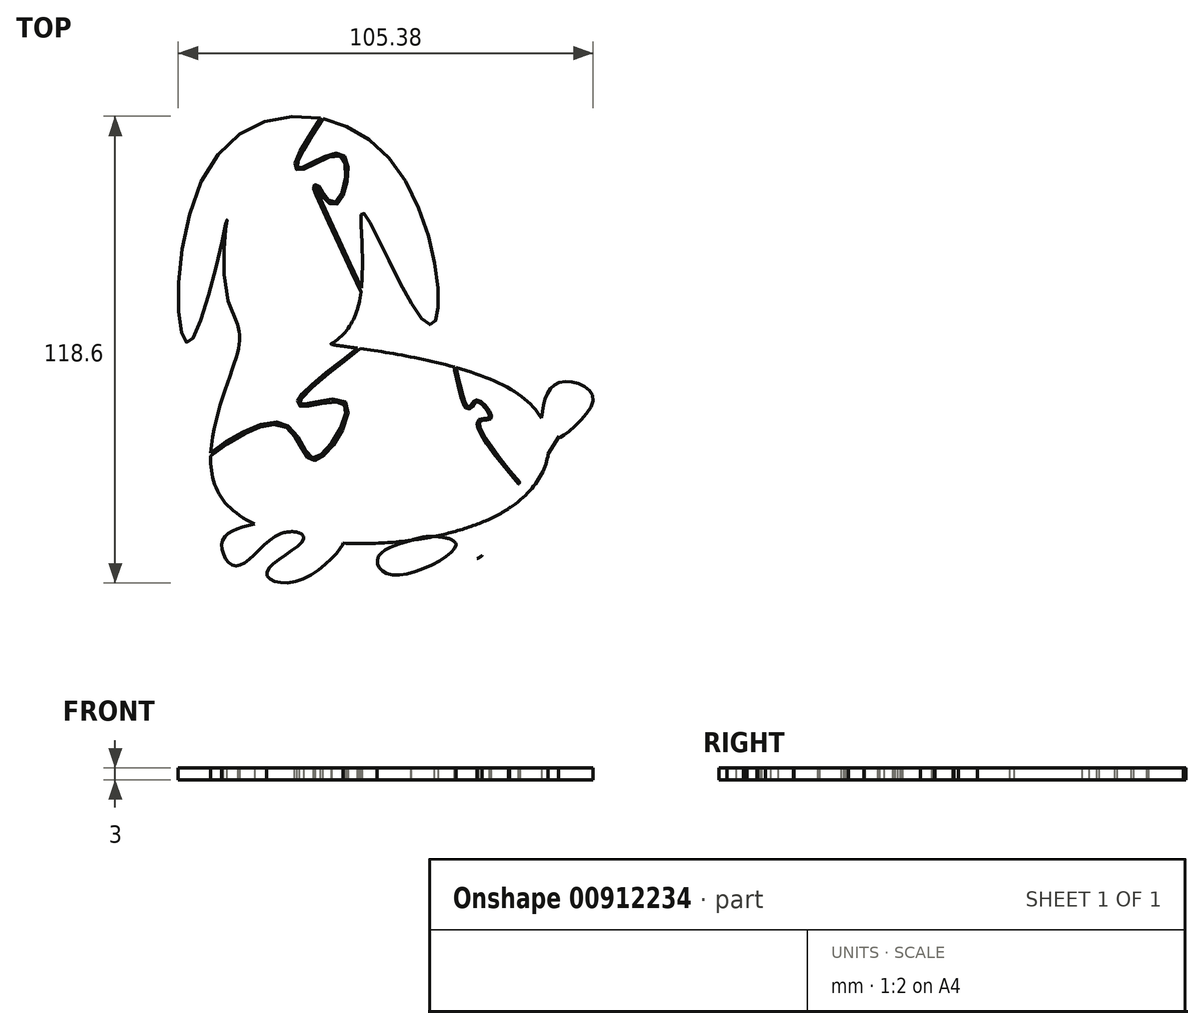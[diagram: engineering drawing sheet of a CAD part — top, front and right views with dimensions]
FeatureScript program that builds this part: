
annotation { "Feature Type Name" : "Feature", "Feature Type Description" : "" }
export const myFeature = defineFeature(function(context is Context, id is Id, definition is map)
    precondition{}
    {
        {
            var Q0;
            Q0=qCreatedBy(makeId("Top.planeOp"),FACE);
            var sketch = newSketch(context, id + "F0", { "sketchPlane" : qUnion([Q0])});
            skFitSpline(sketch, "E0", {"points": [v(-42.08, 41.4) * mm, v(3.83, 40.95) * mm, v(12.83, 0) * mm, v(-3.83, 28.35) * mm, v(-6.98, 0) * mm, v(-35.78, 0) * mm, v(-38.48, 26.55) * mm, v(-47.93, -4.5) * mm, v(-42.08, 41.4) * mm]});
            skFitSpline(sketch, "E1", {"points": [v(-35.78, 0) * mm, v(-35.78, -7.26) * mm, v(-39.63, -44.35) * mm, v(33.41, -46.62) * mm, v(36.82, -18.62) * mm, v(-12.02, -5) * mm, v(-11.88, -4.9) * mm], "startDerivative": vector(15.72, -60) * mm, "endDerivative": vector(20.6, 2.21) * mm});
            skFitSpline(sketch, "E2", {"points": [v(41.44, -23.83) * mm, v(45.9, -14.83) * mm, v(54.6, -19) * mm, v(45.9, -28.84) * mm, v(45.9, -28.46) * mm], "startDerivative": vector(5.67, 39.4) * mm, "endDerivative": vector(3.46, 9.42) * mm});
            skFitSpline(sketch, "E3", {"points": [v(27.3, -49.9) * mm, v(19.79, -56.08) * mm, v(25.08, -59.5) * mm, v(33.41, -46.62) * mm, v(28.87, -54.57) * mm], "startDerivative": vector(-46.04, -22.15) * mm, "endDerivative": vector(-28.83, -55.13) * mm});
            skFitSpline(sketch, "E4", {"points": [v(45.9, -28.46) * mm, v(43.2, -32.87) * mm], "startDerivative": vector(-2.71, -4.4) * mm, "endDerivative": vector(-2.71, -4.4) * mm});
            skFitSpline(sketch, "E5", {"points": [v(8.29, -54.86) * mm, v(0, -59.11) * mm, v(3.51, -63.65) * mm, v(19.79, -56.08) * mm, v(14.24, -53.87) * mm, v(8.29, -54.86) * mm]});
            skFitSpline(sketch, "E6", {"points": [v(-31.44, -50.7) * mm, v(-39.63, -55.33) * mm, v(-36.22, -61.38) * mm, v(-24.7, -53.18) * mm, v(-18.93, -54.48) * mm, v(-28.28, -62.9) * mm, v(-20.33, -65.17) * mm, v(-8.87, -55.58) * mm, v(-9.31, -55.56) * mm], "startDerivative": vector(-84.42, -21.79) * mm, "endDerivative": vector(-21.17, -5.05) * mm});
            skLineSegment(sketch, "E7.bottom", {"start": v(-54.76, 55.76) * mm, "end": v(61.05, 55.76) * mm});
            skLineSegment(sketch, "E7.top", {"start": v(-54.76, -68.06) * mm, "end": v(61.05, -68.06) * mm});
            skLineSegment(sketch, "E7.left", {"start": v(-54.76, 55.76) * mm, "end": v(-54.76, -68.06) * mm});
            skLineSegment(sketch, "E7.right", {"start": v(61.05, 55.76) * mm, "end": v(61.05, -68.06) * mm});
            skFitSpline(sketch, "E8", {"points": [v(28.87, -54.57) * mm, v(25.08, -59.5) * mm, v(19.79, -56.08) * mm], "startDerivative": vector(-6.86, -14.03) * mm, "endDerivative": vector(-11.3, 10.97) * mm});
            skSolve(sketch);
        }
        {
            var Q0;
            {var subQ0=sQuery(id+"F0.wireOp",EDGE,"E1");var subQ1=sQuery(id+"F0.wireOp",EDGE,"E0");var subQ2=makeQuery(id+"F0.imprint","INTERSECT",VERTEX,{"disambiguationData":[OD(0.0)],"derivedFrom":[subQ1,subQ0]});Q0=makeQuery(id+"F0.imprint","IMPRINT",FACE,{"disambiguationData":[TD([[makeQuery(id+"F0.imprint","IMPRINT",EDGE,{"disambiguationData":[TD([[subQ2,1.0]])],"derivedFrom":subQ1}),-1.0]])]});}
            var Q1;
            {var subQ0=sQuery(id+"F0.wireOp",EDGE,"E1");var subQ11=sQuery(id+"F0.wireOp",EDGE,"E0");var subQ12=makeQuery(id+"F0.imprint","INTERSECT",VERTEX,{"disambiguationData":[OD(0.0)],"derivedFrom":[subQ11,subQ0]});Q1=makeQuery(id+"F0.imprint","IMPRINT",FACE,{"disambiguationData":[TD([[makeQuery(id+"F0.imprint","IMPRINT",EDGE,{"disambiguationData":[TD([[subQ12,1.0]])],"derivedFrom":subQ11}),1.0]])]});}
            var Q2;
            {var subQ0=sQuery(id+"F0.wireOp",EDGE,"E6");var subQ1=sQuery(id+"F0.wireOp",EDGE,"E1");var subQ2=makeQuery(id+"F0.imprint","INTERSECT",VERTEX,{"disambiguationData":[OD(0.0)],"derivedFrom":[subQ1,subQ0]});Q2=makeQuery(id+"F0.imprint","IMPRINT",FACE,{"disambiguationData":[TD([[makeQuery(id+"F0.imprint","IMPRINT",EDGE,{"disambiguationData":[TD([[subQ2,-1.0]])],"derivedFrom":subQ1}),-1.0]])]});}
            var Q3;
            {var subQ0=sQuery(id+"F0.wireOp",EDGE,"E6");var subQ1=sQuery(id+"F0.wireOp",EDGE,"E1");var subQ2=makeQuery(id+"F0.imprint","INTERSECT",VERTEX,{"disambiguationData":[OD(1.0)],"derivedFrom":[subQ1,subQ0]});Q3=makeQuery(id+"F0.imprint","IMPRINT",FACE,{"disambiguationData":[TD([[makeQuery(id+"F0.imprint","IMPRINT",EDGE,{"disambiguationData":[TD([[subQ2,1.0]])],"derivedFrom":subQ1}),-1.0]])]});}
            var Q4;
            {var subQ0=sQuery(id+"F0.wireOp",EDGE,"E5");var subQ1=sQuery(id+"F0.wireOp",EDGE,"E1");var subQ2=makeQuery(id+"F0.imprint","INTERSECT",VERTEX,{"disambiguationData":[OD(0.0)],"derivedFrom":[subQ1,subQ0]});Q4=makeQuery(id+"F0.imprint","IMPRINT",FACE,{"disambiguationData":[TD([[makeQuery(id+"F0.imprint","IMPRINT",EDGE,{"disambiguationData":[TD([[subQ2,-1.0]])],"derivedFrom":subQ1}),-1.0]])]});}
            var Q5;
            {var subQ0=sQuery(id+"F0.wireOp",EDGE,"E2");Q5=makeQuery(id+"F0.imprint","IMPRINT",FACE,{"disambiguationData":[TD([[makeQuery(id+"F0.imprint","IMPRINT",EDGE,{"derivedFrom":subQ0}),-1.0]])]});}
            var Q6;
            {var subQ3=sQuery(id+"F0.wireOp",EDGE,"E3");Q6=makeQuery(id+"F0.imprint","IMPRINT",FACE,{"disambiguationData":[TD([[makeQuery(id+"F0.imprint","IMPRINT",EDGE,{"derivedFrom":subQ3}),-1.0]])]});}
            var Q7;
            {var subQ0=sQuery(id+"F0.wireOp",EDGE,"E6");Q7=makeQuery(id+"F0.imprint","IMPRINT",FACE,{"disambiguationData":[TD([[makeQuery(id+"F0.imprint","IMPRINT",EDGE,{"derivedFrom":subQ0}),1.0]])]});}
            extrude(context, id + "F1", {"entities" : qUnion([Q0, Q1, Q2, Q3, Q4, Q5, Q6, Q7]), "depth" : 3 * mm, "offsetDistance" : 25 * mm});
        }
        {
            var Q0;
            Q0=makeQuery(id+"F1.opExtrude","CAP_FACE",FACE,{"disambiguationData":[OSD([sQuery(id+"F0.wireOp",EDGE,"E0"),sQuery(id+"F0.wireOp",EDGE,"E1"),sQuery(id+"F0.wireOp",EDGE,"E2"),sQuery(id+"F0.wireOp",EDGE,"E3"),sQuery(id+"F0.wireOp",EDGE,"E4"),sQuery(id+"F0.wireOp",EDGE,"E5"),sQuery(id+"F0.wireOp",EDGE,"E6"),sQuery(id+"F0.wireOp",EDGE,"E5"),sQuery(id+"F0.wireOp",EDGE,"E3"),sQuery(id+"F0.wireOp",EDGE,"E6"),sQuery(id+"F0.wireOp",EDGE,"E8")])],"isStart":false});
            var sketch = newSketch(context, id + "F2", { "sketchPlane" : qUnion([Q0])});
            skLineSegment(sketch, "E9.bottom", {"start": v(-97.18, -92.65) * mm, "end": v(62.72, -92.65) * mm});
            skLineSegment(sketch, "E9.top", {"start": v(-97.18, 60.2) * mm, "end": v(62.72, 60.2) * mm});
            skLineSegment(sketch, "E9.left", {"start": v(-97.18, -92.65) * mm, "end": v(-97.18, 60.2) * mm});
            skLineSegment(sketch, "E9.right", {"start": v(62.72, -92.65) * mm, "end": v(62.72, 60.2) * mm});
            skPoint(sketch, "E9.middle", {"position": v(-17.23, -16.23) * mm});
            skSolve(sketch);
        }
        {
            var Q0;
            {var subQ4=sQuery(id+"F0.wireOp",EDGE,"E0");Q0=makeQuery(id+"F2.imprint","IMPRINT",FACE,{"disambiguationData":[TD([[makeQuery(id+"F2.imprint","IMPRINT",EDGE,{"derivedFrom":makeQuery(id+"F1.opExtrude","CAP_EDGE",EDGE,{"disambiguationData":[OSD([subQ4])],"isStart":false})}),-1.0]])]});}
            var sketch = newSketch(context, id + "F3", { "sketchPlane" : qUnion([Q0])});
            skFitSpline(sketch, "E10", {"points": [v(-24.72, -56.63) * mm, v(0, -43.73) * mm, v(0, -34.46) * mm, v(10.7, -35.52) * mm, v(8.3, -44.3) * mm, v(35.26, -50.38) * mm], "startDerivative": vector(132, 40.16) * mm, "endDerivative": vector(150.01, -8.59) * mm});
            skFitSpline(sketch, "E11", {"points": [v(-12.2, 55.02) * mm, v(-20.05, 39.72) * mm, v(-8.92, 43.1) * mm, v(-10.95, 30.36) * mm, v(-15.73, 34.82) * mm, v(-3.75, 8.26) * mm], "startDerivative": vector(-69.64, -106.1) * mm, "endDerivative": vector(69.83, -149.18) * mm});
            skFitSpline(sketch, "E12.0", {"points": [v(-12.71, 55.35) * mm, v(-13.44, 54.25) * mm, v(-14.89, 52.04) * mm, v(-16.6, 49.38) * mm, v(-17.84, 47.4) * mm, v(-18.68, 45.99) * mm, v(-19.44, 44.68) * mm, v(-20.08, 43.5) * mm, v(-20.6, 42.43) * mm, v(-20.9, 41.66) * mm, v(-21.08, 41.1) * mm, v(-21.17, 40.72) * mm, v(-21.2, 40.36) * mm, v(-21.19, 40) * mm, v(-21.08, 39.68) * mm, v(-20.9, 39.45) * mm, v(-20.74, 39.3) * mm, v(-20.55, 39.2) * mm, v(-20.28, 39.12) * mm, v(-19.95, 39.11) * mm, v(-19.58, 39.18) * mm, v(-19.2, 39.3) * mm, v(-18.79, 39.45) * mm, v(-18.2, 39.71) * mm, v(-17.39, 40.12) * mm, v(-16.32, 40.68) * mm, v(-15.19, 41.26) * mm, v(-14.03, 41.83) * mm, v(-12.88, 42.33) * mm, v(-11.8, 42.71) * mm, v(-10.8, 42.92) * mm, v(-10.13, 42.93) * mm, v(-9.7, 42.84) * mm, v(-9.42, 42.72) * mm, v(-9.2, 42.56) * mm, v(-8.98, 42.33) * mm, v(-8.79, 42.02) * mm, v(-8.56, 41.5) * mm, v(-8.35, 40.68) * mm, v(-8.24, 39.49) * mm, v(-8.26, 38.17) * mm, v(-8.4, 36.79) * mm, v(-8.67, 35.42) * mm, v(-9.03, 34.11) * mm, v(-9.47, 32.94) * mm, v(-9.98, 31.97) * mm, v(-10.42, 31.4) * mm, v(-10.75, 31.1) * mm, v(-10.97, 30.97) * mm, v(-11.15, 30.92) * mm, v(-11.34, 30.91) * mm, v(-11.56, 30.95) * mm, v(-11.9, 31.1) * mm, v(-12.4, 31.43) * mm, v(-13.01, 32.04) * mm, v(-13.51, 32.65) * mm, v(-13.89, 33.15) * mm, v(-14.15, 33.53) * mm, v(-14.4, 33.89) * mm, v(-14.62, 34.23) * mm, v(-14.79, 34.49) * mm, v(-14.9, 34.68) * mm, v(-15, 34.8) * mm, v(-15.07, 34.92) * mm, v(-15.14, 35.03) * mm, v(-15.2, 35.13) * mm, v(-15.26, 35.2) * mm, v(-15.3, 35.25) * mm, v(-15.34, 35.3) * mm, v(-15.38, 35.34) * mm, v(-15.43, 35.39) * mm, v(-15.5, 35.43) * mm, v(-15.58, 35.48) * mm, v(-15.67, 35.51) * mm, v(-15.79, 35.54) * mm, v(-15.95, 35.54) * mm, v(-16.14, 35.48) * mm, v(-16.29, 35.36) * mm, v(-16.38, 35.23) * mm, v(-16.43, 35.13) * mm, v(-16.45, 35.04) * mm, v(-16.46, 34.95) * mm, v(-16.46, 34.87) * mm, v(-16.46, 34.8) * mm, v(-16.45, 34.75) * mm, v(-16.44, 34.68) * mm, v(-16.41, 34.6) * mm, v(-16.38, 34.5) * mm, v(-16.35, 34.38) * mm, v(-16.3, 34.26) * mm, v(-16.24, 34.07) * mm, v(-16.13, 33.81) * mm, v(-15.98, 33.44) * mm, v(-15.8, 33.02) * mm, v(-15.6, 32.54) * mm, v(-15.38, 32.02) * mm, v(-15.04, 31.25) * mm, v(-14.56, 30.18) * mm, v(-13.9, 28.71) * mm, v(-13.17, 27.1) * mm, v(-12.09, 24.74) * mm, v(-10.58, 21.5) * mm, v(-8.6, 17.2) * mm, v(-6.47, 12.67) * mm, v(-5.02, 9.56) * mm, v(-4.29, 8) * mm]});
            skFitSpline(sketch, "E13.0", {"points": [v(-5.18, -5.94) * mm, v(-6.55, -7) * mm, v(-8.6, -8.6) * mm, v(-11.2, -10.64) * mm, v(-13.06, -12.12) * mm, v(-14.78, -13.53) * mm, v(-16.34, -14.84) * mm, v(-17.7, -16.05) * mm, v(-18.65, -16.96) * mm, v(-19.28, -17.61) * mm, v(-19.69, -18.07) * mm, v(-20.02, -18.5) * mm, v(-20.29, -18.9) * mm, v(-20.45, -19.22) * mm, v(-20.54, -19.5) * mm, v(-20.57, -19.71) * mm, v(-20.57, -19.95) * mm, v(-20.5, -20.2) * mm, v(-20.35, -20.44) * mm, v(-20.16, -20.61) * mm, v(-19.94, -20.73) * mm, v(-19.65, -20.82) * mm, v(-19.28, -20.85) * mm, v(-18.8, -20.84) * mm, v(-18.26, -20.78) * mm, v(-17.66, -20.68) * mm, v(-16.8, -20.53) * mm, v(-15.6, -20.29) * mm, v(-14.08, -20) * mm, v(-12.56, -19.77) * mm, v(-11.13, -19.66) * mm, v(-10.1, -19.72) * mm, v(-9.44, -19.87) * mm, v(-9.04, -20.03) * mm, v(-8.79, -20.2) * mm, v(-8.63, -20.36) * mm, v(-8.5, -20.53) * mm, v(-8.37, -20.8) * mm, v(-8.27, -21.23) * mm, v(-8.24, -21.76) * mm, v(-8.3, -22.58) * mm, v(-8.56, -23.78) * mm, v(-9.13, -25.4) * mm, v(-9.93, -27.07) * mm, v(-10.88, -28.74) * mm, v(-11.95, -30.31) * mm, v(-13.07, -31.7) * mm, v(-14.2, -32.84) * mm, v(-15.08, -33.5) * mm, v(-15.7, -33.8) * mm, v(-16.1, -33.93) * mm, v(-16.42, -33.95) * mm, v(-16.7, -33.9) * mm, v(-16.99, -33.76) * mm, v(-17.4, -33.45) * mm, v(-17.94, -32.82) * mm, v(-18.6, -31.76) * mm, v(-19.28, -30.52) * mm, v(-20.03, -29.19) * mm, v(-20.9, -27.86) * mm, v(-21.9, -26.65) * mm, v(-22.93, -25.8) * mm, v(-23.89, -25.3) * mm, v(-24.68, -25.03) * mm, v(-25.53, -24.87) * mm, v(-26.73, -24.82) * mm, v(-28.32, -25.01) * mm, v(-30.35, -25.57) * mm, v(-32.46, -26.4) * mm, v(-34.61, -27.45) * mm, v(-36.76, -28.66) * mm, v(-38.84, -29.97) * mm, v(-40.8, -31.33) * mm, v(-42.61, -32.7) * mm, v(-43.94, -33.78) * mm, v(-44.87, -34.6) * mm, v(-45.5, -35.18) * mm, v(-46.04, -35.72) * mm, v(-46.5, -36.22) * mm, v(-46.82, -36.6) * mm, v(-47.03, -36.87) * mm, v(-47.16, -37.07) * mm, v(-47.27, -37.27) * mm, v(-47.36, -37.47) * mm, v(-47.42, -37.7) * mm, v(-47.43, -37.92) * mm, v(-47.38, -38.14) * mm, v(-47.27, -38.34) * mm, v(-47.07, -38.53) * mm, v(-46.83, -38.64) * mm, v(-46.62, -38.67) * mm, v(-46.42, -38.68) * mm, v(-46.16, -38.65) * mm, v(-45.85, -38.58) * mm, v(-45.48, -38.45) * mm, v(-45.12, -38.28) * mm, v(-44.84, -38.1) * mm, v(-44.64, -37.92) * mm, v(-44.46, -37.71) * mm, v(-44.29, -37.42) * mm, v(-44.2, -37.04) * mm, v(-44.23, -36.7) * mm, v(-44.3, -36.41) * mm, v(-44.38, -36.15) * mm, v(-44.44, -36) * mm, v(-44.47, -35.93) * mm]});
            skFitSpline(sketch, "E14.0", {"points": [v(-24.89, -56.05) * mm, v(-22.14, -55.22) * mm, v(-18.02, -53.96) * mm, v(-12.95, -52.21) * mm, v(-9.46, -50.84) * mm, v(-6.4, -49.38) * mm, v(-3.85, -47.84) * mm, v(-1.94, -46.2) * mm, v(-1.06, -44.92) * mm, v(-0.7, -44.04) * mm, v(-0.58, -43.6) * mm, v(-0.5, -43.14) * mm, v(-0.44, -42.5) * mm, v(-0.47, -41.68) * mm, v(-0.6, -40.64) * mm, v(-0.82, -39.6) * mm, v(-1.04, -38.55) * mm, v(-1.22, -37.53) * mm, v(-1.32, -36.53) * mm, v(-1.26, -35.57) * mm, v(-1.01, -34.8) * mm, v(-0.64, -34.25) * mm, v(-0.28, -33.88) * mm, v(0.15, -33.58) * mm, v(0.78, -33.24) * mm, v(1.7, -32.93) * mm, v(2.91, -32.72) * mm, v(4.22, -32.63) * mm, v(5.57, -32.68) * mm, v(6.9, -32.86) * mm, v(8.17, -33.16) * mm, v(9.32, -33.58) * mm, v(10.14, -34.05) * mm, v(10.7, -34.52) * mm, v(11.04, -34.9) * mm, v(11.3, -35.36) * mm, v(11.47, -35.85) * mm, v(11.54, -36.35) * mm, v(11.52, -37.02) * mm, v(11.34, -37.85) * mm, v(10.96, -38.84) * mm, v(10.5, -39.83) * mm, v(10, -40.82) * mm, v(9.52, -41.78) * mm, v(9.14, -42.69) * mm, v(8.94, -43.37) * mm, v(8.88, -43.86) * mm, v(8.89, -44.19) * mm, v(8.94, -44.48) * mm, v(9.07, -44.86) * mm, v(9.37, -45.32) * mm, v(9.96, -45.87) * mm, v(10.8, -46.38) * mm, v(12.2, -47.02) * mm, v(14.47, -47.7) * mm, v(17.86, -48.33) * mm, v(21.76, -48.82) * mm, v(27.49, -49.33) * mm, v(32.17, -49.6) * mm, v(35.3, -49.78) * mm]});
            skFitSpline(sketch, "E15", {"points": [v(19.92, -11.48) * mm, v(23.03, -21.02) * mm, v(25.13, -19.17) * mm, v(28.7, -23.9) * mm, v(25.67, -25.06) * mm, v(41.3, -45.88) * mm, v(38.62, -42.15) * mm], "startDerivative": vector(17.03, -73.9) * mm, "endDerivative": vector(3.57, 1.27) * mm});
            skFitSpline(sketch, "E16.0", {"points": [v(19.43, -11.6) * mm, v(19.6, -12.36) * mm, v(19.96, -13.92) * mm, v(20.39, -15.79) * mm, v(20.73, -17.17) * mm, v(20.98, -18.13) * mm, v(21.23, -19) * mm, v(21.48, -19.77) * mm, v(21.7, -20.3) * mm, v(21.88, -20.67) * mm, v(22.02, -20.92) * mm, v(22.18, -21.13) * mm, v(22.36, -21.32) * mm, v(22.6, -21.48) * mm, v(22.86, -21.54) * mm, v(23.08, -21.52) * mm, v(23.3, -21.46) * mm, v(23.49, -21.33) * mm, v(23.66, -21.16) * mm, v(23.81, -20.97) * mm, v(23.95, -20.78) * mm, v(24.13, -20.52) * mm, v(24.36, -20.19) * mm, v(24.6, -19.92) * mm, v(24.77, -19.78) * mm, v(24.9, -19.71) * mm, v(25, -19.67) * mm, v(25.11, -19.66) * mm, v(25.26, -19.69) * mm, v(25.45, -19.75) * mm, v(25.68, -19.87) * mm, v(26.01, -20.08) * mm, v(26.45, -20.45) * mm, v(26.98, -21) * mm, v(27.47, -21.63) * mm, v(27.87, -22.27) * mm, v(28.12, -22.77) * mm, v(28.24, -23.12) * mm, v(28.3, -23.34) * mm, v(28.3, -23.51) * mm, v(28.3, -23.6) * mm, v(28.29, -23.63) * mm, v(28.28, -23.63) * mm, v(28.28, -23.63) * mm, v(28.27, -23.65) * mm, v(28.22, -23.68) * mm, v(28.08, -23.73) * mm, v(27.88, -23.77) * mm, v(27.56, -23.8) * mm, v(27.08, -23.83) * mm, v(26.58, -23.88) * mm, v(26.17, -23.97) * mm, v(25.87, -24.07) * mm, v(25.58, -24.25) * mm, v(25.33, -24.53) * mm, v(25.2, -24.83) * mm, v(25.15, -25.09) * mm, v(25.14, -25.34) * mm, v(25.18, -25.67) * mm, v(25.29, -26.09) * mm, v(25.45, -26.53) * mm, v(25.73, -27.17) * mm, v(26.2, -28.06) * mm, v(26.91, -29.24) * mm, v(27.77, -30.54) * mm, v(29.08, -32.37) * mm, v(30.93, -34.81) * mm, v(32.94, -37.3) * mm, v(34.53, -39.2) * mm, v(35.7, -40.57) * mm, v(36.8, -41.85) * mm, v(37.84, -43.02) * mm, v(38.6, -43.87) * mm, v(39.16, -44.48) * mm, v(39.54, -44.89) * mm, v(39.88, -45.25) * mm, v(40.13, -45.51) * mm, v(40.31, -45.7) * mm, v(40.44, -45.82) * mm, v(40.55, -45.93) * mm, v(40.65, -46.03) * mm, v(40.74, -46.11) * mm, v(40.81, -46.17) * mm, v(40.86, -46.21) * mm, v(40.9, -46.24) * mm, v(40.94, -46.27) * mm, v(40.98, -46.3) * mm, v(41.03, -46.33) * mm, v(41.09, -46.36) * mm, v(41.15, -46.38) * mm, v(41.24, -46.4) * mm, v(41.38, -46.4) * mm, v(41.55, -46.33) * mm, v(41.66, -46.23) * mm, v(41.75, -46.1) * mm, v(41.8, -45.97) * mm, v(41.8, -45.85) * mm, v(41.78, -45.78) * mm, v(41.77, -45.71) * mm, v(41.75, -45.66) * mm, v(41.72, -45.6) * mm, v(41.7, -45.56) * mm, v(41.68, -45.52) * mm, v(41.65, -45.48) * mm, v(41.62, -45.43) * mm, v(41.57, -45.35) * mm, v(41.5, -45.25) * mm, v(41.42, -45.14) * mm, v(41.3, -44.98) * mm, v(41.14, -44.76) * mm, v(40.92, -44.47) * mm, v(40.69, -44.17) * mm, v(40.44, -43.85) * mm, v(40.12, -43.42) * mm, v(39.72, -42.9) * mm, v(39.39, -42.45) * mm, v(39.22, -42.2) * mm, v(39.15, -42.1) * mm, v(39.11, -42.05) * mm, v(39.1, -42.02) * mm, v(39.09, -42) * mm, v(39.09, -42) * mm, v(39.09, -42) * mm, v(39.08, -41.98) * mm, v(39.07, -41.97) * mm, v(39.06, -41.95) * mm, v(39.05, -41.92) * mm, v(39.04, -41.9) * mm, v(39.03, -41.88) * mm]});
            skFitSpline(sketch, "E17", {"points": [v(19.43, -11.6) * mm, v(19.43, -11.31) * mm], "startDerivative": vector(0, 0.29) * mm, "endDerivative": vector(0, 0.29) * mm});
            skFitSpline(sketch, "E18", {"points": [v(-24.89, -56.05) * mm, v(-26.36, -57.99) * mm, v(-26.44, -57.97) * mm], "startDerivative": vector(-2.26, -3.3) * mm, "endDerivative": vector(-0.41, 0.31) * mm});
            skFitSpline(sketch, "E19", {"points": [v(-24.72, -56.63) * mm, v(-25.78, -58.24) * mm, v(-25.82, -58.22) * mm], "startDerivative": vector(-1.62, -2.73) * mm, "endDerivative": vector(-0.24, 0.28) * mm});
            skFitSpline(sketch, "E20", {"points": [v(35.3, -49.78) * mm, v(37.52, -49.94) * mm, v(37.48, -49.9) * mm], "startDerivative": vector(3.77, -0.37) * mm, "endDerivative": vector(-0.44, 0.29) * mm});
            skFitSpline(sketch, "E21", {"points": [v(35.26, -50.38) * mm, v(36.62, -50.53) * mm], "startDerivative": vector(1.36, -0.16) * mm, "endDerivative": vector(1.36, -0.16) * mm});
            skLineSegment(sketch, "E22", {"start": v(-47.4, -37.62) * mm, "end": v(-47.81, -38.38) * mm});
            skFitSpline(sketch, "E23.0", {"points": [v(-4.81, -6.42) * mm, v(-6.18, -7.48) * mm, v(-8.91, -9.6) * mm, v(-12.75, -12.62) * mm, v(-16.05, -15.35) * mm, v(-18.55, -17.64) * mm, v(-19.62, -18.9) * mm, v(-19.92, -19.5) * mm, v(-19.97, -19.72) * mm, v(-19.97, -19.85) * mm, v(-19.95, -19.92) * mm, v(-19.93, -19.98) * mm, v(-19.9, -20.03) * mm, v(-19.85, -20.08) * mm, v(-19.8, -20.12) * mm, v(-19.71, -20.17) * mm, v(-19.54, -20.22) * mm, v(-19.33, -20.25) * mm, v(-19.06, -20.25) * mm, v(-18.76, -20.23) * mm, v(-18.17, -20.16) * mm, v(-17.15, -19.99) * mm, v(-15.25, -19.6) * mm, v(-12.6, -19.1) * mm, v(-10.17, -19.02) * mm, v(-8.72, -19.45) * mm, v(-7.96, -20.1) * mm, v(-7.62, -21.11) * mm, v(-7.65, -22.87) * mm, v(-8.47, -25.6) * mm, v(-10, -28.52) * mm, v(-11.47, -30.67) * mm, v(-12.62, -32.1) * mm, v(-13.8, -33.29) * mm, v(-14.94, -34.14) * mm, v(-15.82, -34.5) * mm, v(-16.45, -34.55) * mm, v(-16.9, -34.46) * mm, v(-17.31, -34.27) * mm, v(-17.83, -33.87) * mm, v(-18.43, -33.16) * mm, v(-19.12, -32.06) * mm, v(-19.81, -30.8) * mm, v(-20.55, -29.5) * mm, v(-21.38, -28.22) * mm, v(-22.34, -27.07) * mm, v(-23.46, -26.15) * mm, v(-24.8, -25.56) * mm, v(-26.4, -25.39) * mm, v(-28.2, -25.6) * mm, v(-30.15, -26.14) * mm, v(-32.22, -26.95) * mm, v(-35.04, -28.32) * mm, v(-38.56, -30.44) * mm, v(-41.72, -32.74) * mm, v(-43.82, -34.46) * mm, v(-45.12, -35.63) * mm, v(-46.1, -36.64) * mm, v(-46.57, -37.23) * mm, v(-46.74, -37.54) * mm, v(-46.79, -37.65) * mm, v(-46.81, -37.73) * mm, v(-46.82, -37.79) * mm, v(-46.83, -37.84) * mm, v(-46.82, -37.88) * mm, v(-46.81, -37.93) * mm, v(-46.8, -37.96) * mm, v(-46.77, -37.99) * mm, v(-46.73, -38.02) * mm, v(-46.7, -38.04) * mm, v(-46.66, -38.05) * mm, v(-46.61, -38.06) * mm, v(-46.54, -38.07) * mm, v(-46.44, -38.08) * mm, v(-46.27, -38.06) * mm, v(-45.92, -37.99) * mm, v(-45.5, -37.8) * mm, v(-45.16, -37.58) * mm, v(-44.97, -37.4) * mm, v(-44.86, -37.2) * mm, v(-44.81, -37) * mm, v(-44.82, -36.8) * mm, v(-44.88, -36.5) * mm, v(-44.97, -36.3) * mm, v(-45.03, -36.15) * mm]});
            skLineSegment(sketch, "E24", {"start": v(19.92, -11.48) * mm, "end": v(19.44, -9.05) * mm});
            skLineSegment(sketch, "E25", {"start": v(19.43, -11.31) * mm, "end": v(18.9, -8.6) * mm});
            skLineSegment(sketch, "E26", {"start": v(-4.81, -6.42) * mm, "end": v(-1.7, -3.92) * mm});
            skLineSegment(sketch, "E27", {"start": v(-5.18, -5.94) * mm, "end": v(-2.35, -3.47) * mm});
            skLineSegment(sketch, "E28", {"start": v(-4.29, 8) * mm, "end": v(-3.98, 7.38) * mm});
            skFitSpline(sketch, "E29.0", {"points": [v(-35.78, 0) * mm, v(-35.31, -1.79) * mm, v(-33.78, -7.62) * mm, v(-60.27, -59.22) * mm, v(41.98, -58.93) * mm, v(49.35, -9.83) * mm, v(-13.43, -5.55) * mm, v(-11.97, -4.92) * mm, v(-11.88, -4.9) * mm]});
            skFitSpline(sketch, "E30.0.0", {"points": [v(-42.08, 41.4) * mm, v(-31.2, 57.22) * mm, v(13.25, 55.63) * mm, v(19.77, -26.88) * mm, v(-11, 50.67) * mm, v(3.7, -9.9) * mm, v(-45.62, -9.94) * mm, v(-33.93, 49.01) * mm, v(-51.15, -34.45) * mm, v(-53, 25.53) * mm, v(-42.08, 41.4) * mm]});
            skFitSpline(sketch, "E30.0.1", {"points": [v(-11.88, -4.9) * mm, v(-11.97, -4.92) * mm, v(-13.43, -5.55) * mm, v(49.35, -9.83) * mm, v(41.98, -58.93) * mm, v(-60.27, -59.22) * mm, v(-33.78, -7.62) * mm, v(-35.31, -1.79) * mm, v(-35.78, 0) * mm]});
            skFitSpline(sketch, "E30.0.2", {"points": [v(41.44, -23.83) * mm, v(42, -19.87) * mm, v(43.33, -11.95) * mm, v(61.23, -17.78) * mm, v(45.37, -29.91) * mm, v(45.83, -28.64) * mm, v(45.9, -28.46) * mm]});
            skFitSpline(sketch, "E30.0.3", {"points": [v(45.9, -28.46) * mm, v(45, -29.93) * mm, v(44.1, -31.4) * mm, v(43.2, -32.87) * mm]});
            skFitSpline(sketch, "E30.0.4", {"points": [v(-11.88, -4.9) * mm, v(-11.97, -4.92) * mm, v(-13.43, -5.55) * mm, v(49.35, -9.83) * mm, v(41.98, -58.93) * mm, v(-60.27, -59.22) * mm, v(-33.78, -7.62) * mm, v(-35.31, -1.79) * mm, v(-35.78, 0) * mm]});
            skFitSpline(sketch, "E30.0.5", {"points": [v(27.3, -49.9) * mm, v(23.48, -51.73) * mm, v(16.63, -55.07) * mm, v(26.52, -64.33) * mm, v(36.5, -40) * mm, v(31.18, -50.15) * mm, v(28.87, -54.57) * mm]});
            skFitSpline(sketch, "E30.0.6", {"points": [v(28.87, -54.57) * mm, v(27.73, -56.9) * mm, v(25.44, -61.57) * mm, v(21.68, -57.92) * mm, v(19.79, -56.08) * mm]});
            skFitSpline(sketch, "E30.0.7", {"points": [v(8.29, -54.86) * mm, v(10.6, -54.2) * mm, v(13.2, -53.37) * mm, v(25.73, -55.55) * mm, v(2.79, -67.5) * mm, v(-2.45, -57.82) * mm, v(5.42, -55.68) * mm, v(8.29, -54.86) * mm]});
            skFitSpline(sketch, "E30.0.8", {"points": [v(-11.88, -4.9) * mm, v(-11.97, -4.92) * mm, v(-13.43, -5.55) * mm, v(49.35, -9.83) * mm, v(41.98, -58.93) * mm, v(-60.27, -59.22) * mm, v(-33.78, -7.62) * mm, v(-35.31, -1.79) * mm, v(-35.78, 0) * mm]});
            skFitSpline(sketch, "E30.0.9", {"points": [v(-9.31, -55.56) * mm, v(-9.1, -55.51) * mm, v(-7.7, -55.13) * mm, v(-18.91, -68.55) * mm, v(-34.1, -63.16) * mm, v(-13.9, -54.28) * mm, v(-26.72, -50.62) * mm, v(-35.85, -66.31) * mm, v(-42.24, -53.48) * mm, v(-35.22, -51.67) * mm, v(-31.44, -50.7) * mm]});
            skFitSpline(sketch, "E30.0.10", {"points": [v(-11.88, -4.9) * mm, v(-11.97, -4.92) * mm, v(-13.43, -5.55) * mm, v(49.35, -9.83) * mm, v(41.98, -58.93) * mm, v(-60.27, -59.22) * mm, v(-33.78, -7.62) * mm, v(-35.31, -1.79) * mm, v(-35.78, 0) * mm]});
            skFitSpline(sketch, "E30.0.11", {"points": [v(-9.31, -55.56) * mm, v(-9.1, -55.51) * mm, v(-7.7, -55.13) * mm, v(-18.91, -68.55) * mm, v(-34.1, -63.16) * mm, v(-13.9, -54.28) * mm, v(-26.72, -50.62) * mm, v(-35.85, -66.31) * mm, v(-42.24, -53.48) * mm, v(-35.22, -51.67) * mm, v(-31.44, -50.7) * mm]});
            skFitSpline(sketch, "E30.0.12", {"points": [v(-11.88, -4.9) * mm, v(-11.97, -4.92) * mm, v(-13.43, -5.55) * mm, v(49.35, -9.83) * mm, v(41.98, -58.93) * mm, v(-60.27, -59.22) * mm, v(-33.78, -7.62) * mm, v(-35.31, -1.79) * mm, v(-35.78, 0) * mm]});
            skSolve(sketch);
        }
        {
            var Q0;
            {var subQ5=sQuery(id+"F3.wireOp",EDGE,"E17");Q0=makeQuery(id+"F3.imprint","IMPRINT",FACE,{"disambiguationData":[TD([[makeQuery(id+"F3.imprint","IMPRINT",EDGE,{"derivedFrom":subQ5}),-1.0]])]});}
            var Q1;
            {var subQ3=sQuery(id+"F3.wireOp",EDGE,"E10");var subQ5=sQuery(id+"F3.wireOp",EDGE,"E30.0.5");var subQ9=makeQuery(id+"F3.imprint","INTERSECT",VERTEX,{"derivedFrom":[subQ3,subQ5]});Q1=makeQuery(id+"F3.imprint","IMPRINT",FACE,{"disambiguationData":[TD([[makeQuery(id+"F3.imprint","IMPRINT",EDGE,{"disambiguationData":[TD([[subQ9,1.0]])],"derivedFrom":subQ3}),1.0]])]});}
            var Q2;
            {var subQ0=sQuery(id+"F3.wireOp",EDGE,"E30.0.1");var subQ1=sQuery(id+"F3.wireOp",EDGE,"E13.0");var subQ2=makeQuery(id+"F3.imprint","INTERSECT",VERTEX,{"derivedFrom":[subQ1,subQ0]});Q2=makeQuery(id+"F3.imprint","IMPRINT",FACE,{"disambiguationData":[TD([[makeQuery(id+"F3.imprint","IMPRINT",EDGE,{"disambiguationData":[TD([[subQ2,-1.0]])],"derivedFrom":subQ1}),1.0]])]});}
            var Q3;
            {var subQ0=sQuery(id+"F3.wireOp",EDGE,"E30.0.0");var subQ1=sQuery(id+"F3.wireOp",EDGE,"E11");var subQ2=makeQuery(id+"F3.imprint","INTERSECT",VERTEX,{"disambiguationData":[OD(0.0)],"derivedFrom":[subQ1,subQ0]});Q3=makeQuery(id+"F3.imprint","IMPRINT",FACE,{"disambiguationData":[TD([[makeQuery(id+"F3.imprint","IMPRINT",EDGE,{"disambiguationData":[TD([[subQ2,-1.0]])],"derivedFrom":subQ1}),-1.0]])]});}
            extrude(context, id + "F4", {"entities" : qUnion([Q0, Q1, Q2, Q3]), "operationType" : NewBodyOperationType.REMOVE, "oppositeDirection" : true, "depth" : 25 * mm, "offsetDistance" : 25 * mm});
        }
    });
